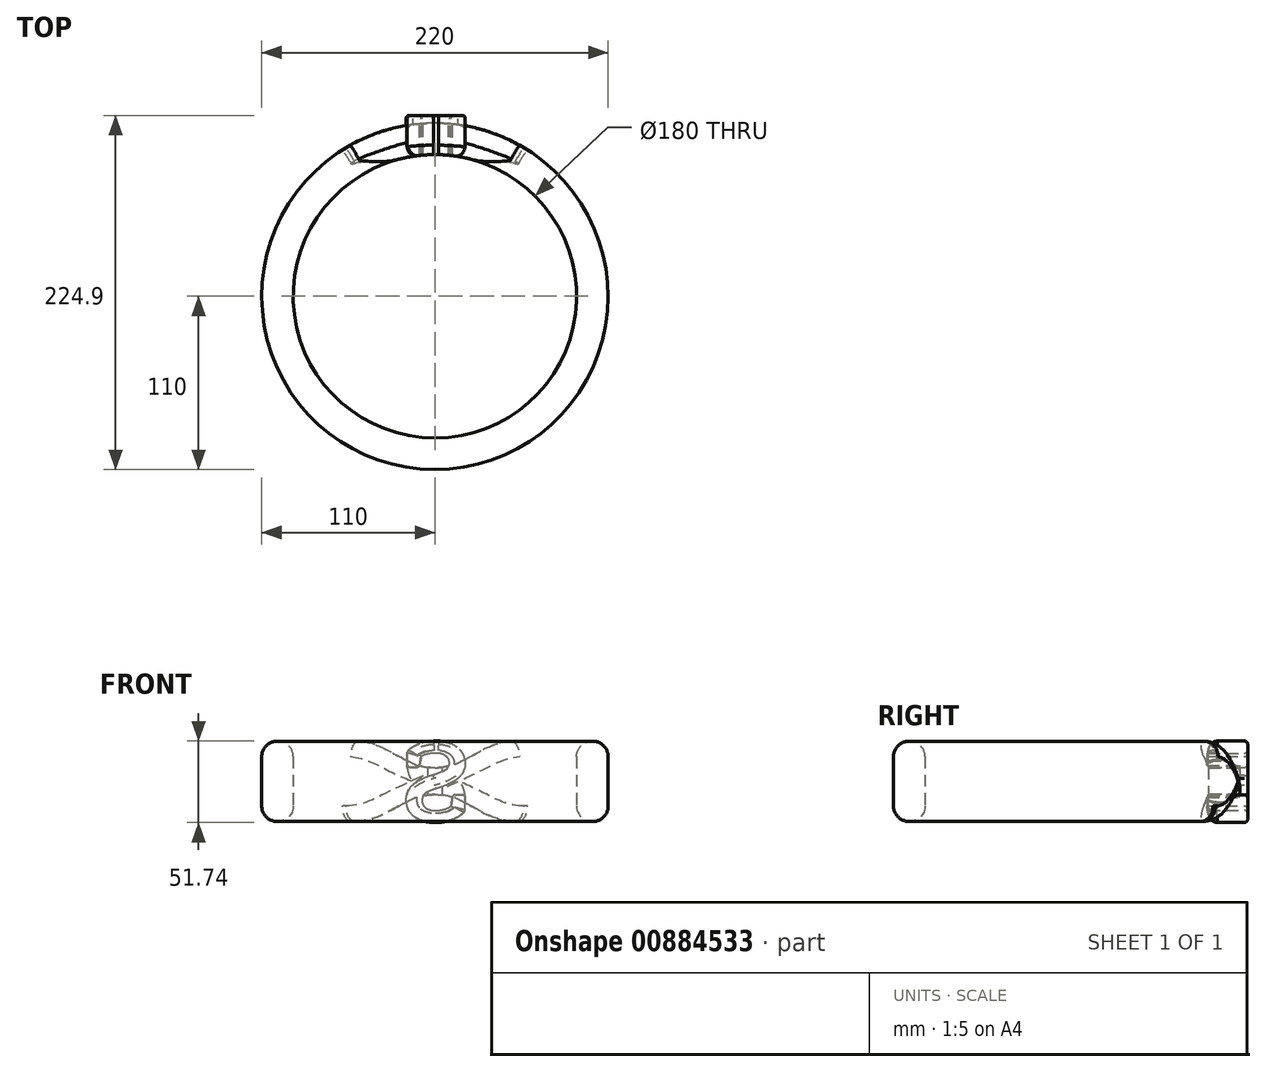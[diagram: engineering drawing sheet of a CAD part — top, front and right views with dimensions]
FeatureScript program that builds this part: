
annotation { "Feature Type Name" : "Feature", "Feature Type Description" : "" }
export const myFeature = defineFeature(function(context is Context, id is Id, definition is map)
    precondition{}
    {
        {
            var Q0;
            Q0=qCreatedBy(makeId("Top.planeOp"),FACE);
            var sketch = newSketch(context, id + "F0", { "sketchPlane" : qUnion([Q0])});
            skCircle(sketch, "E0", {"center": v(0, 0) * mm, "radius": 110 * mm});
            skCircle(sketch, "E1", {"center": v(0, 0) * mm, "radius": 90 * mm});
            skPoint(sketch, "E2", {"position": v(0, 110) * mm});
            skLineSegment(sketch, "E3", {"start": v(45.83, 109.9) * mm, "end": v(-45.83, 109.9) * mm});
            skSolve(sketch);
        }
        {
            var Q0;
            {var subQ4=sQuery(id+"F0.wireOp",EDGE,"E1");Q0=makeQuery(id+"F0.imprint","IMPRINT",FACE,{"disambiguationData":[TD([[makeQuery(id+"F0.imprint","IMPRINT",EDGE,{"derivedFrom":subQ4}),-1.0]])]});}
            extrude(context, id + "F1", {"entities" : qUnion([Q0]), "depth" : 51 * mm, "offsetDistance" : 25 * mm});
        }
        {
            var Q0;
            Q0=makeQuery(id+"F1.opExtrude","SWEPT_FACE",FACE,{"disambiguationData":[OSD([sQuery(id+"F0.wireOp",EDGE,"E3")])]});
            cPlane(context, id + "F2", {"entities" : qUnion([Q0]), "cplaneType" : CPlaneType.OFFSET, "offset" : 0 * mm, "width" : 150 * mm, "height" : 150 * mm});
        }
        {
            var Q0;
            Q0=qCreatedBy(id+"F2.planeOp",FACE);
            var sketch = newSketch(context, id + "F3", { "sketchPlane" : qUnion([Q0])});
            skFitSpline(sketch, "E4.MirrorCS", {"points": [v(0, 34.1) * mm, v(-51.2, 51.1) * mm], "startDerivative": vector(-60.93, 0) * mm, "endDerivative": vector(-65.59, 0.6) * mm});
            skFitSpline(sketch, "E5.MirrorCS", {"points": [v(0, 17.1) * mm, v(-51.2, 0.1) * mm], "startDerivative": vector(-60.93, 0) * mm, "endDerivative": vector(-65.59, -0.6) * mm});
            skLineSegment(sketch, "E6", {"start": v(0, 34.1) * mm, "end": v(0, 17.1) * mm});
            skFitSpline(sketch, "E7.MirrorCS", {"points": [v(0, 17.1) * mm, v(51.2, 0.1) * mm], "startDerivative": vector(60.93, 0) * mm, "endDerivative": vector(65.59, -0.6) * mm});
            skFitSpline(sketch, "E8.MirrorCS", {"points": [v(0, 34.1) * mm, v(51.2, 51.1) * mm], "startDerivative": vector(60.93, 0) * mm, "endDerivative": vector(65.59, 0.6) * mm});
            skLineSegment(sketch, "E9", {"start": v(51.2, 51.1) * mm, "end": v(74.52, 51.1) * mm});
            skLineSegment(sketch, "E10.MirrorCS", {"start": v(51.2, 0.1) * mm, "end": v(74.52, 0.1) * mm});
            skLineSegment(sketch, "E11.MirrorCS", {"start": v(-51.2, 51.1) * mm, "end": v(-74.52, 51.1) * mm});
            skLineSegment(sketch, "E12.MirrorCS", {"start": v(-51.2, 0.1) * mm, "end": v(-74.52, 0.1) * mm});
            skText(sketch, "E13", { "text": "S", "fontName": "RobotoSlab-Bold.ttf"});
            skLineSegment(sketch, "E14", {"start": v(-74.52, 51.1) * mm, "end": v(-74.52, 0.1) * mm});
            skLineSegment(sketch, "E15", {"start": v(74.52, 51.1) * mm, "end": v(74.52, 0.1) * mm});
            skLineSegment(sketch, "E16", {"start": v(-51.2, 51.1) * mm, "end": v(51.2, 51.1) * mm});
            skFitSpline(sketch, "E17", {"points": [v(-51.2, 51.1) * mm, v(-74.84, 54.06) * mm, v(-76.44, 56.31) * mm], "startDerivative": vector(-41.16, 2.13) * mm, "endDerivative": vector(-3.1, 9.48) * mm});
            skFitSpline(sketch, "E18.MirrorCS", {"points": [v(51.2, 51.1) * mm, v(74.84, 54.06) * mm, v(76.44, 56.31) * mm], "startDerivative": vector(41.16, 2.13) * mm, "endDerivative": vector(3.1, 9.48) * mm});
            skLineSegment(sketch, "E19", {"start": v(-22.63, 25.6) * mm, "end": v(-48.99, 25.6) * mm, "construction": true});
            skFitSpline(sketch, "E20.MirrorCS", {"points": [v(51.2, 0.1) * mm, v(74.84, -2.84) * mm, v(76.44, -5.1) * mm], "startDerivative": vector(41.16, -2.13) * mm, "endDerivative": vector(3.1, -9.48) * mm});
            skFitSpline(sketch, "E21.MirrorCS", {"points": [v(-51.2, 0.1) * mm, v(-74.84, -2.84) * mm, v(-76.44, -5.1) * mm], "startDerivative": vector(-41.16, -2.13) * mm, "endDerivative": vector(-3.1, -9.48) * mm});
            skLineSegment(sketch, "E22", {"start": v(-76.44, 56.31) * mm, "end": v(76.44, 56.31) * mm});
            skLineSegment(sketch, "E23", {"start": v(-76.44, -5.1) * mm, "end": v(76.44, -5.1) * mm});
            const initialGuessF3  = {"E13": [-0.02263, 0.0001, 1, 0, 0.051]};
            skSetInitialGuess(sketch, initialGuessF3);
            skSolve(sketch);
        }
        {
            var Q0;
            {var subQ3=sQuery(id+"F3.wireOp",EDGE,"E13.sketch_text.stroke-25");var subQ5=sQuery(id+"F3.wireOp",EDGE,"E13.sketch_text.stroke-26");var subQ6=makeQuery(id+"F3.imprint","INTERSECT",VERTEX,{"derivedFrom":[subQ3,subQ5]});Q0=makeQuery(id+"F3.imprint","IMPRINT",FACE,{"disambiguationData":[TD([[makeQuery(id+"F3.imprint","IMPRINT",EDGE,{"disambiguationData":[TD([[subQ6,1.0]])],"derivedFrom":subQ3}),1.0]])]});}
            var Q1;
            {var subQ1=sQuery(id+"F3.wireOp",EDGE,"E13.sketch_text.stroke-28");Q1=makeQuery(id+"F3.imprint","IMPRINT",FACE,{"disambiguationData":[TD([[makeQuery(id+"F3.imprint","IMPRINT",EDGE,{"derivedFrom":subQ1}),1.0]])]});}
            var Q2;
            {var subQ0=sQuery(id+"F3.wireOp",EDGE,"E13.sketch_text.stroke-2");Q2=makeQuery(id+"F3.imprint","IMPRINT",FACE,{"disambiguationData":[TD([[makeQuery(id+"F3.imprint","IMPRINT",EDGE,{"derivedFrom":subQ0}),1.0]])]});}
            var Q3;
            {var subQ0=sQuery(id+"F3.wireOp",EDGE,"E13.sketch_text.stroke-17");Q3=makeQuery(id+"F3.imprint","IMPRINT",FACE,{"disambiguationData":[TD([[makeQuery(id+"F3.imprint","IMPRINT",EDGE,{"derivedFrom":subQ0}),1.0]])]});}
            var Q4;
            {var subQ0=sQuery(id+"F3.wireOp",EDGE,"E13.sketch_text.stroke-11");Q4=makeQuery(id+"F3.imprint","IMPRINT",FACE,{"disambiguationData":[TD([[makeQuery(id+"F3.imprint","IMPRINT",EDGE,{"derivedFrom":subQ0}),1.0]])]});}
            extrude(context, id + "F4", {"entities" : qUnion([Q0, Q1, Q2, Q3, Q4]), "operationType" : NewBodyOperationType.REMOVE, "oppositeDirection" : true, "depth" : 40 * mm, "offsetDistance" : 25 * mm});
        }
        {
            var Q0;
            {var subQ7=sQuery(id+"F3.wireOp",EDGE,"E13.sketch_text.stroke-11");Q0=makeQuery(id+"F3.imprint","IMPRINT",FACE,{"disambiguationData":[TD([[makeQuery(id+"F3.imprint","IMPRINT",EDGE,{"derivedFrom":subQ7}),-1.0]])]});}
            var Q1;
            {var subQ10=sQuery(id+"F3.wireOp",EDGE,"E13.sketch_text.stroke-2");Q1=makeQuery(id+"F3.imprint","IMPRINT",FACE,{"disambiguationData":[TD([[makeQuery(id+"F3.imprint","IMPRINT",EDGE,{"derivedFrom":subQ10}),-1.0]])]});}
            var Q2;
            {var subQ0=sQuery(id+"F3.wireOp",EDGE,"E13.sketch_text.stroke-8");Q2=makeQuery(id+"F3.imprint","IMPRINT",FACE,{"disambiguationData":[TD([[makeQuery(id+"F3.imprint","IMPRINT",EDGE,{"derivedFrom":subQ0}),-1.0]])]});}
            var Q3;
            {var subQ5=sQuery(id+"F3.wireOp",EDGE,"E13.sketch_text.stroke-23");Q3=makeQuery(id+"F3.imprint","IMPRINT",FACE,{"disambiguationData":[TD([[makeQuery(id+"F3.imprint","IMPRINT",EDGE,{"derivedFrom":subQ5}),-1.0]])]});}
            var Q4;
            {var subQ5=sQuery(id+"F3.wireOp",EDGE,"E13.sketch_text.stroke-15");Q4=makeQuery(id+"F3.imprint","IMPRINT",FACE,{"disambiguationData":[TD([[makeQuery(id+"F3.imprint","IMPRINT",EDGE,{"derivedFrom":subQ5}),-1.0]])]});}
            var Q5;
            {var subQ5=sQuery(id+"F3.wireOp",EDGE,"E13.sketch_text.stroke-0");Q5=makeQuery(id+"F3.imprint","IMPRINT",FACE,{"disambiguationData":[TD([[makeQuery(id+"F3.imprint","IMPRINT",EDGE,{"derivedFrom":subQ5}),-1.0]])]});}
            var Q6;
            Q6=makeQuery(id+"F1.opExtrude","SWEPT_FACE",FACE,{"disambiguationData":[OSD([sQuery(id+"F0.wireOp",EDGE,"E1")])]});
            extrude(context, id + "F5", {"entities" : qUnion([Q0, Q1, Q2, Q3, Q4, Q5]), "operationType" : NewBodyOperationType.ADD, "endBound" : BoundingType.UP_TO_SURFACE, "oppositeDirection" : true, "depth" : 10 * mm, "endBoundEntityFace" : qUnion([Q6]), "offsetDistance" : 25 * mm});
        }
        {
            var Q0;
            {var subQ10=sQuery(id+"F3.wireOp",EDGE,"E13.sketch_text.stroke-2");Q0=makeQuery(id+"F3.imprint","IMPRINT",FACE,{"disambiguationData":[TD([[makeQuery(id+"F3.imprint","IMPRINT",EDGE,{"derivedFrom":subQ10}),-1.0]])]});}
            var Q1;
            {var subQ5=sQuery(id+"F3.wireOp",EDGE,"E13.sketch_text.stroke-0");Q1=makeQuery(id+"F3.imprint","IMPRINT",FACE,{"disambiguationData":[TD([[makeQuery(id+"F3.imprint","IMPRINT",EDGE,{"derivedFrom":subQ5}),-1.0]])]});}
            var Q2;
            {var subQ5=sQuery(id+"F3.wireOp",EDGE,"E13.sketch_text.stroke-23");Q2=makeQuery(id+"F3.imprint","IMPRINT",FACE,{"disambiguationData":[TD([[makeQuery(id+"F3.imprint","IMPRINT",EDGE,{"derivedFrom":subQ5}),-1.0]])]});}
            var Q3;
            {var subQ0=sQuery(id+"F3.wireOp",EDGE,"E13.sketch_text.stroke-8");Q3=makeQuery(id+"F3.imprint","IMPRINT",FACE,{"disambiguationData":[TD([[makeQuery(id+"F3.imprint","IMPRINT",EDGE,{"derivedFrom":subQ0}),-1.0]])]});}
            var Q4;
            {var subQ7=sQuery(id+"F3.wireOp",EDGE,"E13.sketch_text.stroke-11");Q4=makeQuery(id+"F3.imprint","IMPRINT",FACE,{"disambiguationData":[TD([[makeQuery(id+"F3.imprint","IMPRINT",EDGE,{"derivedFrom":subQ7}),-1.0]])]});}
            var Q5;
            {var subQ5=sQuery(id+"F3.wireOp",EDGE,"E13.sketch_text.stroke-15");Q5=makeQuery(id+"F3.imprint","IMPRINT",FACE,{"disambiguationData":[TD([[makeQuery(id+"F3.imprint","IMPRINT",EDGE,{"derivedFrom":subQ5}),-1.0]])]});}
            extrude(context, id + "F6", {"entities" : qUnion([Q0, Q1, Q2, Q3, Q4, Q5]), "operationType" : NewBodyOperationType.ADD, "depth" : 5 * mm, "offsetDistance" : 25 * mm});
        }
        {
            var Q0;
            {var subQ0=sQuery(id+"F0.wireOp",EDGE,"E1");var subQ2=sQuery(id+"F3.wireOp",EDGE,"E4.MirrorCS");Q0=makeQuery(id+"F4.boolean.opBoolean","SPLIT",EDGE,{"disambiguationData":[TD([makeQuery(id+"F4.opExtrude","SWEPT_FACE",FACE,{"disambiguationData":[OSD([subQ2]),TDD([makeQuery(id+"F3.imprint","IMPRINT",EDGE,{"disambiguationData":[TD([[makeQuery(id+"F3.imprint","INTERSECT",VERTEX,{"derivedFrom":[subQ2,sQuery(id+"F3.wireOp",EDGE,"E13.sketch_text.stroke-25")]}),-1.0]])],"derivedFrom":subQ2})])]})])],"derivedFrom":makeQuery(id+"F1.opExtrude","CAP_EDGE",EDGE,{"disambiguationData":[OSD([subQ0])],"isStart":false})});}
            var Q1;
            {var subQ0=sQuery(id+"F0.wireOp",EDGE,"E1");Q1=makeQuery(id+"F4.boolean.opBoolean","SPLIT",EDGE,{"disambiguationData":[TD([makeQuery(id+"F4.opExtrude","SWEPT_FACE",FACE,{"disambiguationData":[OSD([sQuery(id+"F3.wireOp",EDGE,"E20.MirrorCS")])]})])],"derivedFrom":makeQuery(id+"F1.opExtrude","CAP_EDGE",EDGE,{"disambiguationData":[OSD([subQ0])],"isStart":true})});}
            var Q2;
            Q2=makeQuery(id+"F1.opExtrude","CAP_EDGE",EDGE,{"disambiguationData":[OSD([sQuery(id+"F0.wireOp",EDGE,"E0")])],"isStart":false});
            var Q3;
            {var subQ0=sQuery(id+"F0.wireOp",EDGE,"E0");Q3=makeQuery(id+"F4.boolean.opBoolean","SPLIT",EDGE,{"disambiguationData":[TD([makeQuery(id+"F4.opExtrude","SWEPT_FACE",FACE,{"disambiguationData":[OSD([sQuery(id+"F3.wireOp",EDGE,"E20.MirrorCS")])]})])],"derivedFrom":makeQuery(id+"F1.opExtrude","CAP_EDGE",EDGE,{"disambiguationData":[OSD([subQ0])],"isStart":true})});}
            var Q4;
            {var subQ0=sQuery(id+"F3.wireOp",EDGE,"E5.MirrorCS");Q4=makeQuery(id+"F4.boolean.opBoolean","INTERSECT",EDGE,{"derivedFrom":[makeQuery(id+"F1.opExtrude","SWEPT_FACE",FACE,{"disambiguationData":[OSD([sQuery(id+"F0.wireOp",EDGE,"E0")])]}),makeQuery(id+"F4.opExtrude","SWEPT_FACE",FACE,{"disambiguationData":[OSD([subQ0]),TDD([makeQuery(id+"F3.imprint","IMPRINT",EDGE,{"disambiguationData":[TD([[makeQuery(id+"F3.imprint","INTERSECT",VERTEX,{"derivedFrom":[subQ0,sQuery(id+"F3.wireOp",EDGE,"E13.sketch_text.stroke-14")]}),-1.0]])],"derivedFrom":subQ0})])]})]});}
            var Q5;
            {var subQ0=sQuery(id+"F3.wireOp",EDGE,"E4.MirrorCS");Q5=makeQuery(id+"F4.boolean.opBoolean","INTERSECT",EDGE,{"derivedFrom":[makeQuery(id+"F1.opExtrude","SWEPT_FACE",FACE,{"disambiguationData":[OSD([sQuery(id+"F0.wireOp",EDGE,"E0")])]}),makeQuery(id+"F4.opExtrude","SWEPT_FACE",FACE,{"disambiguationData":[OSD([subQ0]),TDD([makeQuery(id+"F3.imprint","IMPRINT",EDGE,{"disambiguationData":[TD([[makeQuery(id+"F3.imprint","INTERSECT",VERTEX,{"derivedFrom":[subQ0,sQuery(id+"F3.wireOp",EDGE,"E13.sketch_text.stroke-25")]}),-1.0]])],"derivedFrom":subQ0})])]})]});}
            var Q6;
            {var subQ0=sQuery(id+"F3.wireOp",EDGE,"E8.MirrorCS");Q6=makeQuery(id+"F4.boolean.opBoolean","INTERSECT",EDGE,{"derivedFrom":[makeQuery(id+"F1.opExtrude","SWEPT_FACE",FACE,{"disambiguationData":[OSD([sQuery(id+"F0.wireOp",EDGE,"E0")])]}),makeQuery(id+"F4.opExtrude","SWEPT_FACE",FACE,{"disambiguationData":[OSD([subQ0]),TDD([makeQuery(id+"F3.imprint","IMPRINT",EDGE,{"disambiguationData":[TD([[makeQuery(id+"F3.imprint","INTERSECT",VERTEX,{"derivedFrom":[subQ0,sQuery(id+"F3.wireOp",EDGE,"E13.sketch_text.stroke-29")]}),-1.0]])],"derivedFrom":subQ0})])]})]});}
            var Q7;
            {var subQ0=sQuery(id+"F3.wireOp",EDGE,"E7.MirrorCS");Q7=makeQuery(id+"F4.boolean.opBoolean","INTERSECT",EDGE,{"derivedFrom":[makeQuery(id+"F1.opExtrude","SWEPT_FACE",FACE,{"disambiguationData":[OSD([sQuery(id+"F0.wireOp",EDGE,"E0")])]}),makeQuery(id+"F4.opExtrude","SWEPT_FACE",FACE,{"disambiguationData":[OSD([subQ0]),TDD([makeQuery(id+"F3.imprint","IMPRINT",EDGE,{"disambiguationData":[TD([[makeQuery(id+"F3.imprint","INTERSECT",VERTEX,{"derivedFrom":[subQ0,sQuery(id+"F3.wireOp",EDGE,"E13.sketch_text.stroke-10")]}),-1.0]])],"derivedFrom":subQ0})])]})]});}
            fillet(context, id + "F7", {"entities" : qUnion([Q0, Q1, Q2, Q3, Q4, Q5, Q6, Q7]), "radius" : 9.8 * mm, "tangentPropagation" : true, "allowEdgeOverflow" : false});
        }
        {
            var Q0;
            Q0=makeQuery(id+"F6.opExtrude","SWEPT_EDGE",EDGE,{"disambiguationData":[OSD([sQuery(id+"F3.wireOp",EDGE,"E13.sketch_text.stroke-15"),sQuery(id+"F3.wireOp",EDGE,"E13.sketch_text.stroke-16")])]});
            var Q1;
            Q1=makeQuery(id+"F6.opExtrude","SWEPT_EDGE",EDGE,{"disambiguationData":[OSD([sQuery(id+"F3.wireOp",EDGE,"E13.sketch_text.stroke-14"),sQuery(id+"F3.wireOp",EDGE,"E13.sketch_text.stroke-15")])]});
            var Q2;
            {var subQ0=sQuery(id+"F3.wireOp",EDGE,"E13.sketch_text.stroke-14");var subQ1=sQuery(id+"F3.wireOp",EDGE,"E13.sketch_text.stroke-13");Q2=makeQuery(id+"F6.boolean.opBoolean","MERGE",EDGE,{"derivedFrom":[makeQuery(id+"F5.boolean.opBoolean","MERGE",EDGE,{"derivedFrom":[makeQuery(id+"F4.boolean.opBoolean","COPY",EDGE,{"derivedFrom":makeQuery(id+"F4.opExtrude","SWEPT_EDGE",EDGE,{"disambiguationData":[OSD([subQ1,subQ0])]})}),makeQuery(id+"F5.opExtrude","SWEPT_EDGE",EDGE,{"disambiguationData":[OSD([subQ1,subQ0])]})]}),makeQuery(id+"F6.opExtrude","SWEPT_EDGE",EDGE,{"disambiguationData":[OSD([subQ1,subQ0])]})]});}
            var Q3;
            {var subQ0=sQuery(id+"F3.wireOp",EDGE,"E13.sketch_text.stroke-29");var subQ1=sQuery(id+"F3.wireOp",EDGE,"E13.sketch_text.stroke-28");Q3=makeQuery(id+"F6.boolean.opBoolean","MERGE",EDGE,{"derivedFrom":[makeQuery(id+"F5.boolean.opBoolean","MERGE",EDGE,{"derivedFrom":[makeQuery(id+"F4.boolean.opBoolean","COPY",EDGE,{"derivedFrom":makeQuery(id+"F4.opExtrude","SWEPT_EDGE",EDGE,{"disambiguationData":[OSD([subQ1,subQ0])]})}),makeQuery(id+"F5.opExtrude","SWEPT_EDGE",EDGE,{"disambiguationData":[OSD([subQ1,subQ0])]})]}),makeQuery(id+"F6.opExtrude","SWEPT_EDGE",EDGE,{"disambiguationData":[OSD([subQ1,subQ0])]})]});}
            var Q4;
            Q4=makeQuery(id+"F6.opExtrude","SWEPT_EDGE",EDGE,{"disambiguationData":[OSD([sQuery(id+"F3.wireOp",EDGE,"E13.sketch_text.stroke-0"),sQuery(id+"F3.wireOp",EDGE,"E13.sketch_text.stroke-29")])]});
            var Q5;
            Q5=makeQuery(id+"F6.opExtrude","SWEPT_EDGE",EDGE,{"disambiguationData":[OSD([sQuery(id+"F3.wireOp",EDGE,"E13.sketch_text.stroke-0"),sQuery(id+"F3.wireOp",EDGE,"E13.sketch_text.stroke-1")])]});
            fillet(context, id + "F8", {"entities" : qUnion([Q0, Q1, Q2, Q3, Q4, Q5]), "radius" : 2 * mm, "tangentPropagation" : true, "allowEdgeOverflow" : false});
        }
        {
            var Q0;
            Q0=makeQuery(id+"F6.opExtrude","CAP_FACE",FACE,{"disambiguationData":[OSD([sQuery(id+"F3.wireOp",EDGE,"E13.sketch_text.stroke-0"),sQuery(id+"F3.wireOp",EDGE,"E13.sketch_text.stroke-1"),sQuery(id+"F3.wireOp",EDGE,"E13.sketch_text.stroke-2"),sQuery(id+"F3.wireOp",EDGE,"E13.sketch_text.stroke-3"),sQuery(id+"F3.wireOp",EDGE,"E13.sketch_text.stroke-4"),sQuery(id+"F3.wireOp",EDGE,"E13.sketch_text.stroke-5"),sQuery(id+"F3.wireOp",EDGE,"E13.sketch_text.stroke-6"),sQuery(id+"F3.wireOp",EDGE,"E13.sketch_text.stroke-7"),sQuery(id+"F3.wireOp",EDGE,"E13.sketch_text.stroke-8"),sQuery(id+"F3.wireOp",EDGE,"E13.sketch_text.stroke-9"),sQuery(id+"F3.wireOp",EDGE,"E13.sketch_text.stroke-10"),sQuery(id+"F3.wireOp",EDGE,"E13.sketch_text.stroke-11"),sQuery(id+"F3.wireOp",EDGE,"E13.sketch_text.stroke-12"),sQuery(id+"F3.wireOp",EDGE,"E13.sketch_text.stroke-13"),sQuery(id+"F3.wireOp",EDGE,"E13.sketch_text.stroke-14"),sQuery(id+"F3.wireOp",EDGE,"E13.sketch_text.stroke-15"),sQuery(id+"F3.wireOp",EDGE,"E13.sketch_text.stroke-16"),sQuery(id+"F3.wireOp",EDGE,"E13.sketch_text.stroke-17"),sQuery(id+"F3.wireOp",EDGE,"E13.sketch_text.stroke-18"),sQuery(id+"F3.wireOp",EDGE,"E13.sketch_text.stroke-19"),sQuery(id+"F3.wireOp",EDGE,"E13.sketch_text.stroke-20"),sQuery(id+"F3.wireOp",EDGE,"E13.sketch_text.stroke-21"),sQuery(id+"F3.wireOp",EDGE,"E13.sketch_text.stroke-22"),sQuery(id+"F3.wireOp",EDGE,"E13.sketch_text.stroke-23"),sQuery(id+"F3.wireOp",EDGE,"E13.sketch_text.stroke-24"),sQuery(id+"F3.wireOp",EDGE,"E13.sketch_text.stroke-25"),sQuery(id+"F3.wireOp",EDGE,"E13.sketch_text.stroke-26"),sQuery(id+"F3.wireOp",EDGE,"E13.sketch_text.stroke-27"),sQuery(id+"F3.wireOp",EDGE,"E13.sketch_text.stroke-28"),sQuery(id+"F3.wireOp",EDGE,"E13.sketch_text.stroke-29"),sQuery(id+"F3.wireOp",EDGE,"E16")])],"isStart":false});
            fillet(context, id + "F9", {"entities" : qUnion([Q0]), "radius" : 2 * mm, "tangentPropagation" : true, "allowEdgeOverflow" : false});
        }
        {
            var Q0;
            Q0=makeQuery(id+"F7.opFillet","TWEAK_EDGE",EDGE,{"derivedFrom":[makeQuery(id+"F5.boolean.opBoolean","INTERSECT",VERTEX,{"derivedFrom":[makeQuery(id+"F1.opExtrude","SWEPT_FACE",FACE,{"disambiguationData":[OSD([sQuery(id+"F0.wireOp",EDGE,"E0")])]}),makeQuery(id+"F5.opExtrude","SWEPT_FACE",FACE,{"disambiguationData":[OSD([sQuery(id+"F3.wireOp",EDGE,"E13.sketch_text.stroke-0")])]}),makeQuery(id+"F5.opExtrude","SWEPT_FACE",FACE,{"disambiguationData":[OSD([sQuery(id+"F3.wireOp",EDGE,"E13.sketch_text.stroke-29")])]})]})]});
            var Q1;
            Q1=makeQuery(id+"F7.opFillet","TWEAK_EDGE",EDGE,{"derivedFrom":[makeQuery(id+"F5.boolean.opBoolean","INTERSECT",VERTEX,{"derivedFrom":[makeQuery(id+"F1.opExtrude","SWEPT_FACE",FACE,{"disambiguationData":[OSD([sQuery(id+"F0.wireOp",EDGE,"E0")])]}),makeQuery(id+"F5.opExtrude","SWEPT_FACE",FACE,{"disambiguationData":[OSD([sQuery(id+"F3.wireOp",EDGE,"E13.sketch_text.stroke-14")])]}),makeQuery(id+"F5.opExtrude","SWEPT_FACE",FACE,{"disambiguationData":[OSD([sQuery(id+"F3.wireOp",EDGE,"E13.sketch_text.stroke-15")])]})]})]});
            fillet(context, id + "F10", {"entities" : qUnion([Q0, Q1]), "radius" : 3 * mm, "tangentPropagation" : true, "allowEdgeOverflow" : false});
        }
        {
            var Q0;
            {var subQ0=sQuery(id+"F3.wireOp",EDGE,"E13.sketch_text.stroke-12");Q0=makeQuery(id+"F5.boolean.opBoolean","MERGE",EDGE,{"derivedFrom":[makeQuery(id+"F4.boolean.opBoolean","INTERSECT",EDGE,{"derivedFrom":[makeQuery(id+"F1.opExtrude","SWEPT_FACE",FACE,{"disambiguationData":[OSD([sQuery(id+"F0.wireOp",EDGE,"E1")])]}),makeQuery(id+"F4.opExtrude","SWEPT_FACE",FACE,{"disambiguationData":[OSD([subQ0])]})]}),makeQuery(id+"F5.opExtrude","CAP_EDGE",EDGE,{"disambiguationData":[OSD([subQ0])],"isStart":false})]});}
            var Q1;
            Q1=makeQuery(id+"F5.opExtrude","CAP_EDGE",EDGE,{"disambiguationData":[OSD([sQuery(id+"F3.wireOp",EDGE,"E16")])],"isStart":false});
            var Q2;
            Q2=makeQuery(id+"F4.boolean.opBoolean","INTERSECT",EDGE,{"derivedFrom":[makeQuery(id+"F1.opExtrude","SWEPT_FACE",FACE,{"disambiguationData":[OSD([sQuery(id+"F0.wireOp",EDGE,"E1")])]}),makeQuery(id+"F4.opExtrude","SWEPT_FACE",FACE,{"disambiguationData":[OSD([sQuery(id+"F3.wireOp",EDGE,"E13.sketch_text.stroke-28")])]})]});
            var Q3;
            Q3=makeQuery(id+"F4.boolean.opBoolean","INTERSECT",EDGE,{"derivedFrom":[makeQuery(id+"F1.opExtrude","SWEPT_FACE",FACE,{"disambiguationData":[OSD([sQuery(id+"F0.wireOp",EDGE,"E1")])]}),makeQuery(id+"F4.opExtrude","SWEPT_FACE",FACE,{"disambiguationData":[OSD([sQuery(id+"F3.wireOp",EDGE,"E13.sketch_text.stroke-25")])]})]});
            fillet(context, id + "F11", {"entities" : qUnion([Q0, Q1, Q2, Q3]), "radius" : 6 * mm, "tangentPropagation" : true, "allowEdgeOverflow" : false});
        }
    });
